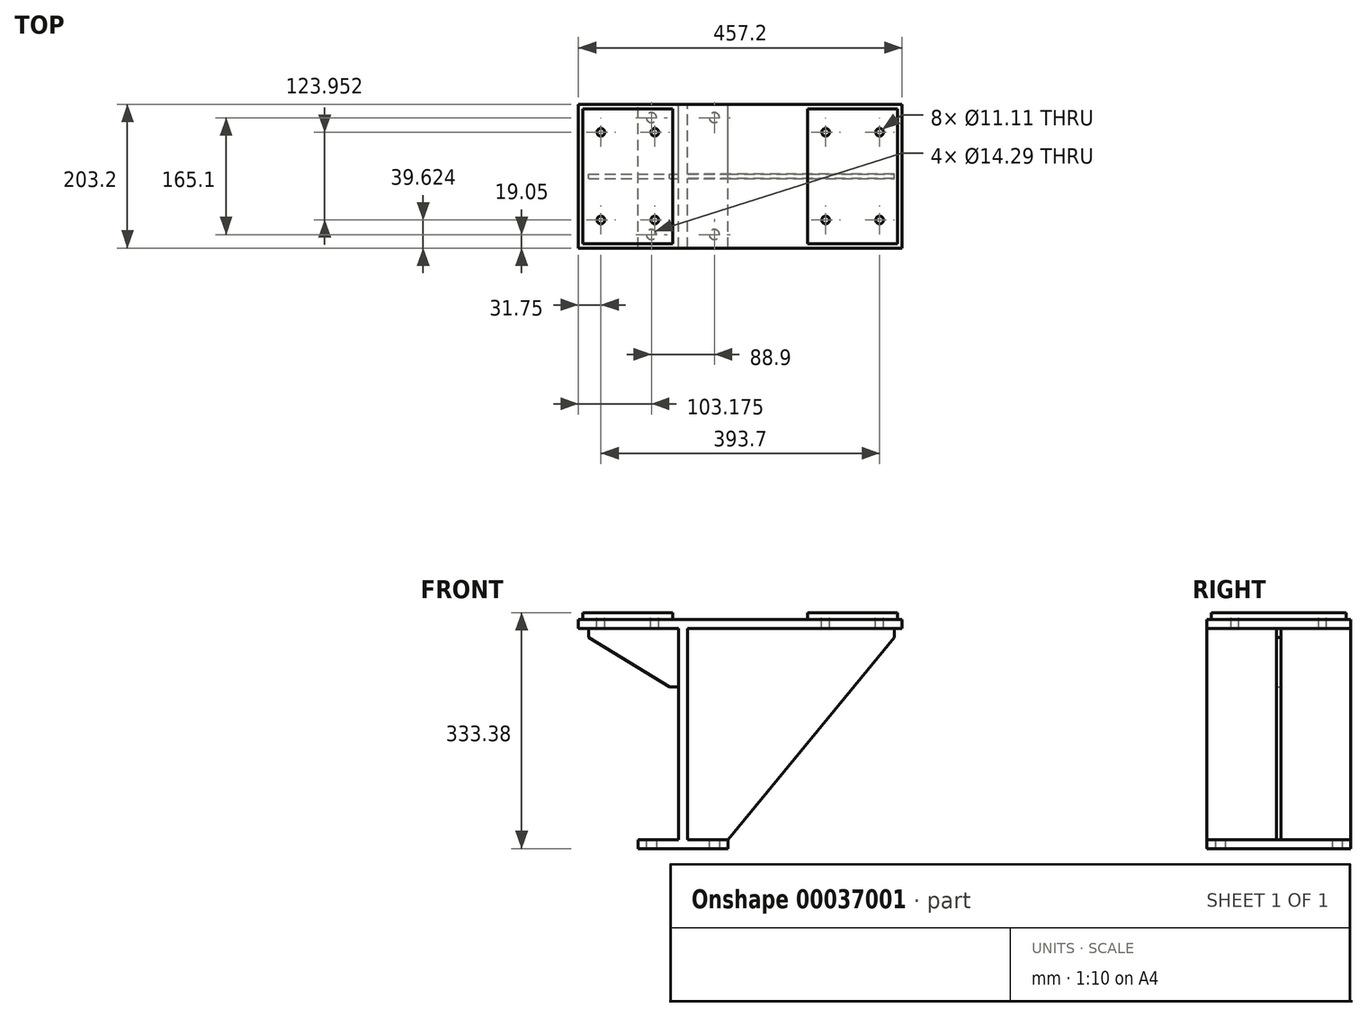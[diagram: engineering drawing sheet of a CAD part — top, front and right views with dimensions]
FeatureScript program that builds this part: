
annotation { "Feature Type Name" : "Feature", "Feature Type Description" : "" }
export const myFeature = defineFeature(function(context is Context, id is Id, definition is map)
    precondition{}
    {
        {
            var Q0;
            Q0=qCreatedBy(makeId("Top.planeOp"),FACE);
            var sketch = newSketch(context, id + "F0", { "sketchPlane" : qUnion([Q0])});
            skLineSegment(sketch, "E0.rect.bottom", {"start": v(-228.6, 101.6) * mm, "end": v(228.6, 101.6) * mm});
            skLineSegment(sketch, "E0.rect.top", {"start": v(-228.6, -101.6) * mm, "end": v(228.6, -101.6) * mm});
            skLineSegment(sketch, "E0.rect.left", {"start": v(-228.6, 101.6) * mm, "end": v(-228.6, -101.6) * mm});
            skLineSegment(sketch, "E0.rect.right", {"start": v(228.6, 101.6) * mm, "end": v(228.6, -101.6) * mm});
            skPoint(sketch, "E0.rect.middle", {"position": v(0, 0) * mm});
            skSolve(sketch);
        }
        {
            var Q0;
            Q0 = qSketchRegion(id + "F0", true);
            extrude(context, id + "F1", {"entities" : qUnion([Q0]), "oppositeDirection" : true, "depth" : 12.7 * mm});
        }
        {
            var Q0;
            Q0=makeQuery(id+"F1.opExtrude","CAP_FACE",FACE,{"disambiguationData":[OSD([sQuery(id+"F0.wireOp",EDGE,"E0.rect.bottom"),sQuery(id+"F0.wireOp",EDGE,"E0.rect.top"),sQuery(id+"F0.wireOp",EDGE,"E0.rect.left"),sQuery(id+"F0.wireOp",EDGE,"E0.rect.right")])],"isStart":true});
            var sketch = newSketch(context, id + "F2", { "sketchPlane" : qUnion([Q0])});
            skLineSegment(sketch, "E1.0", {"start": v(222.25, 95.25) * mm, "end": v(95.25, 95.25) * mm});
            skLineSegment(sketch, "E1.1", {"start": v(222.25, -95.25) * mm, "end": v(222.25, 95.25) * mm});
            skLineSegment(sketch, "E1.2", {"start": v(-222.25, -95.25) * mm, "end": v(-95.25, -95.25) * mm});
            skLineSegment(sketch, "E1.3", {"start": v(-222.25, 95.25) * mm, "end": v(-222.25, -95.25) * mm});
            skLineSegment(sketch, "E2.0", {"start": v(95.25, -95.25) * mm, "end": v(95.25, 95.25) * mm});
            skLineSegment(sketch, "E3.0", {"start": v(-95.25, 95.25) * mm, "end": v(-95.25, -95.25) * mm});
            skLineSegment(sketch, "E4.trimOffspring", {"start": v(-95.25, 95.25) * mm, "end": v(-222.25, 95.25) * mm});
            skLineSegment(sketch, "E5.trimOffspring", {"start": v(95.25, -95.25) * mm, "end": v(222.25, -95.25) * mm});
            skSolve(sketch);
        }
        {
            var Q0;
            Q0 = qSketchRegion(id + "F2", true);
            extrude(context, id + "F3", {"entities" : qUnion([Q0]), "operationType" : NewBodyOperationType.ADD, "depth" : 9.52 * mm});
        }
        {
            var Q0;
            Q0=makeQuery(id+"F3.opExtrude","CAP_FACE",FACE,{"disambiguationData":[OSD([sQuery(id+"F2.wireOp",EDGE,"E1.2"),sQuery(id+"F2.wireOp",EDGE,"E1.3"),sQuery(id+"F2.wireOp",EDGE,"E3.0"),sQuery(id+"F2.wireOp",EDGE,"E4.trimOffspring")])],"isStart":false});
            var sketch = newSketch(context, id + "F4", { "sketchPlane" : qUnion([Q0])});
            skLineSegment(sketch, "E6", {"start": v(-222.25, 0) * mm, "end": v(243.7, 0) * mm, "construction": true});
            skPoint(sketch, "E6.endSnap0", {"position": v(-95.25, 0) * mm});
            skLineSegment(sketch, "E7", {"start": v(-158.75, -95.25) * mm, "end": v(-158.75, 95.25) * mm, "construction": true});
            skLineSegment(sketch, "E8.0.0", {"start": v(222.25, -95.25) * mm, "end": v(222.25, 95.25) * mm, "construction": true});
            skLineSegment(sketch, "E8.0.1", {"start": v(222.25, 95.25) * mm, "end": v(95.25, 95.25) * mm, "construction": true});
            skLineSegment(sketch, "E8.0.2", {"start": v(95.25, 95.25) * mm, "end": v(95.25, -95.25) * mm, "construction": true});
            skLineSegment(sketch, "E8.0.3", {"start": v(95.25, -95.25) * mm, "end": v(222.25, -95.25) * mm, "construction": true});
            skLineSegment(sketch, "E9", {"start": v(158.75, -95.25) * mm, "end": v(158.75, 95.25) * mm, "construction": true});
            skLineSegment(sketch, "E10.0", {"start": v(-222.25, 61.98) * mm, "end": v(243.7, 61.98) * mm, "construction": true});
            skLineSegment(sketch, "E11.0", {"start": v(-222.25, -61.98) * mm, "end": v(243.7, -61.98) * mm, "construction": true});
            skLineSegment(sketch, "E12.0", {"start": v(-196.85, -95.25) * mm, "end": v(-196.85, 95.25) * mm, "construction": true});
            skLineSegment(sketch, "E13.0", {"start": v(-120.65, -95.25) * mm, "end": v(-120.65, 95.25) * mm, "construction": true});
            skLineSegment(sketch, "E14.0", {"start": v(120.65, -95.25) * mm, "end": v(120.65, 95.25) * mm, "construction": true});
            skLineSegment(sketch, "E15.0", {"start": v(196.85, -95.25) * mm, "end": v(196.85, 95.25) * mm, "construction": true});
            skPoint(sketch, "E16", {"position": v(-196.85, 61.98) * mm});
            skPoint(sketch, "E17", {"position": v(-120.65, 61.98) * mm});
            skPoint(sketch, "E18", {"position": v(-120.65, -61.98) * mm});
            skPoint(sketch, "E19", {"position": v(-196.85, -61.98) * mm});
            skPoint(sketch, "E20", {"position": v(120.65, 61.98) * mm});
            skPoint(sketch, "E21", {"position": v(196.85, 61.98) * mm});
            skPoint(sketch, "E22", {"position": v(196.85, -61.98) * mm});
            skPoint(sketch, "E23", {"position": v(120.65, -61.98) * mm});
            skSolve(sketch);
        }
        {
            var Q0;
            Q0=sQuery(id+"F4.wireOp",VERTEX,"E16");
            var Q1;
            Q1=sQuery(id+"F4.wireOp",VERTEX,"E17");
            var Q2;
            Q2=sQuery(id+"F4.wireOp",VERTEX,"E19");
            var Q3;
            Q3=sQuery(id+"F4.wireOp",VERTEX,"E18");
            var Q4;
            Q4=sQuery(id+"F4.wireOp",VERTEX,"E20");
            var Q5;
            Q5=sQuery(id+"F4.wireOp",VERTEX,"E21");
            var Q6;
            Q6=sQuery(id+"F4.wireOp",VERTEX,"E23");
            var Q7;
            Q7=sQuery(id+"F4.wireOp",VERTEX,"E22");
            var Q8;
            Q8=makeQuery(id+"F1.opExtrude","SWEPT_BODY",BODY,{"disambiguationData":[OSD([sQuery(id+"F0.wireOp",EDGE,"E0.rect.bottom"),sQuery(id+"F0.wireOp",EDGE,"E0.rect.top"),sQuery(id+"F0.wireOp",EDGE,"E0.rect.left"),sQuery(id+"F0.wireOp",EDGE,"E0.rect.right")])]});
            hole(context, id + "F5", {"style" : HoleStyle.SIMPLE, "holeDiameter" : 11.1 * mm, "endStyle" : HoleEndStyle.THROUGH, "locations" : qUnion([Q0, Q1, Q2, Q3, Q4, Q5, Q6, Q7]), "scope" : qUnion([Q8])});
        }
        {
            var Q0;
            Q0=qCreatedBy(makeId("Front.planeOp"),FACE);
            var sketch = newSketch(context, id + "F6", { "sketchPlane" : qUnion([Q0])});
            skLineSegment(sketch, "E24.0", {"start": v(-228.6, -12.7) * mm, "end": v(-228.6, 0) * mm, "construction": true});
            skLineSegment(sketch, "E25.0", {"start": v(-228.6, -12.7) * mm, "end": v(228.6, -12.7) * mm, "construction": true});
            skLineSegment(sketch, "E26", {"start": v(-228.6, -12.7) * mm, "end": v(-228.6, -311.15) * mm, "construction": true});
            skLineSegment(sketch, "E27.0", {"start": v(-80.98, -12.7) * mm, "end": v(-80.98, -311.15) * mm, "construction": true});
            skLineSegment(sketch, "E28.0", {"start": v(-87.33, -12.7) * mm, "end": v(-87.33, -311.15) * mm});
            skLineSegment(sketch, "E29.0", {"start": v(-74.63, -12.7) * mm, "end": v(-74.63, -311.15) * mm});
            skLineSegment(sketch, "E30.0", {"start": v(-214.33, -12.7) * mm, "end": v(-214.33, -25.4) * mm});
            skLineSegment(sketch, "E31.0", {"start": v(-228.6, -25.4) * mm, "end": v(-214.33, -25.4) * mm});
            skLineSegment(sketch, "E32.0", {"start": v(-228.6, -95.25) * mm, "end": v(-214.33, -95.25) * mm});
            skLineSegment(sketch, "E33", {"start": v(-214.33, -25.4) * mm, "end": v(-100.03, -95.25) * mm});
            skLineSegment(sketch, "E34.trimOffspring", {"start": v(-100.03, -95.25) * mm, "end": v(-87.33, -95.25) * mm});
            skLineSegment(sketch, "E35.trimOffspring", {"start": v(-214.33, -95.25) * mm, "end": v(-214.33, -311.15) * mm});
            skLineSegment(sketch, "E36", {"start": v(-214.33, -12.7) * mm, "end": v(-87.33, -12.7) * mm});
            skSolve(sketch);
        }
        {
            var Q0;
            Q0 = qSketchRegion(id + "F6", true);
            extrude(context, id + "F7", {"entities" : qUnion([Q0]), "operationType" : NewBodyOperationType.ADD, "endBound" : BoundingType.SYMMETRIC, "depth" : 6.35 * mm});
        }
        {
            var Q0;
            Q0=qCreatedBy(makeId("Front.planeOp"),FACE);
            var sketch = newSketch(context, id + "F8", { "sketchPlane" : qUnion([Q0])});
            skLineSegment(sketch, "E37.0", {"start": v(217.47, -12.7) * mm, "end": v(217.47, -311.15) * mm});
            skLineSegment(sketch, "E38.0", {"start": v(-74.63, -12.7) * mm, "end": v(-74.63, -311.15) * mm});
            skLineSegment(sketch, "E39.0", {"start": v(-17.48, -12.7) * mm, "end": v(-17.48, -311.15) * mm});
            skLineSegment(sketch, "E40.0", {"start": v(-228.6, -25.4) * mm, "end": v(228.6, -25.4) * mm});
            skLineSegment(sketch, "E41", {"start": v(-74.63, -311.15) * mm, "end": v(-17.48, -311.15) * mm});
            skLineSegment(sketch, "E42", {"start": v(-17.48, -311.15) * mm, "end": v(217.47, -25.4) * mm});
            skLineSegment(sketch, "E43", {"start": v(217.47, -25.4) * mm, "end": v(217.47, -12.7) * mm});
            skLineSegment(sketch, "E44", {"start": v(217.47, -12.7) * mm, "end": v(-74.63, -12.7) * mm});
            skSolve(sketch);
        }
        {
            var Q0;
            Q0 = qSketchRegion(id + "F8", true);
            extrude(context, id + "F9", {"entities" : qUnion([Q0]), "operationType" : NewBodyOperationType.ADD, "endBound" : BoundingType.SYMMETRIC, "depth" : 6.35 * mm});
        }
        {
            var Q0;
            Q0=qCreatedBy(makeId("Front.planeOp"),FACE);
            var sketch = newSketch(context, id + "F10", { "sketchPlane" : qUnion([Q0])});
            skLineSegment(sketch, "E45.0", {"start": v(-74.63, -12.7) * mm, "end": v(-74.63, -311.15) * mm});
            skLineSegment(sketch, "E46.0", {"start": v(-87.33, -12.7) * mm, "end": v(-87.33, -311.15) * mm});
            skLineSegment(sketch, "E47.0", {"start": v(-228.6, -12.7) * mm, "end": v(228.6, -12.7) * mm});
            skLineSegment(sketch, "E48", {"start": v(-87.33, -311.15) * mm, "end": v(-74.63, -311.15) * mm});
            skSolve(sketch);
        }
        {
            var Q0;
            Q0 = qSketchRegion(id + "F10", true);
            extrude(context, id + "F11", {"entities" : qUnion([Q0]), "operationType" : NewBodyOperationType.ADD, "endBound" : BoundingType.SYMMETRIC, "depth" : 203.2 * mm});
        }
        {
            var Q0;
            Q0=qCreatedBy(makeId("Front.planeOp"),FACE);
            var sketch = newSketch(context, id + "F12", { "sketchPlane" : qUnion([Q0])});
            skLineSegment(sketch, "E49.0", {"start": v(-74.63, -311.15) * mm, "end": v(-17.48, -311.15) * mm});
            skLineSegment(sketch, "E50.bottom", {"start": v(-17.48, -311.15) * mm, "end": v(-144.48, -311.15) * mm});
            skLineSegment(sketch, "E50.top", {"start": v(-17.48, -323.85) * mm, "end": v(-144.48, -323.85) * mm});
            skLineSegment(sketch, "E50.left", {"start": v(-17.48, -311.15) * mm, "end": v(-17.48, -323.85) * mm});
            skLineSegment(sketch, "E50.right", {"start": v(-144.48, -311.15) * mm, "end": v(-144.48, -323.85) * mm});
            skSolve(sketch);
        }
        {
            var Q0;
            Q0 = qSketchRegion(id + "F12", true);
            extrude(context, id + "F13", {"entities" : qUnion([Q0]), "operationType" : NewBodyOperationType.ADD, "endBound" : BoundingType.SYMMETRIC, "depth" : 203.2 * mm});
        }
        {
            var Q0;
            Q0=makeQuery(id+"F13.opExtrude","SWEPT_FACE",FACE,{"disambiguationData":[OSD([sQuery(id+"F12.wireOp",EDGE,"E50.top")])]});
            var sketch = newSketch(context, id + "F14", { "sketchPlane" : qUnion([Q0])});
            skLineSegment(sketch, "E51", {"start": v(-80.98, 101.6) * mm, "end": v(-80.98, -101.6) * mm, "construction": true});
            skLineSegment(sketch, "E52", {"start": v(-230.25, 0) * mm, "end": v(5.19, 0) * mm, "construction": true});
            skLineSegment(sketch, "E53.0", {"start": v(-125.43, 101.6) * mm, "end": v(-125.43, -101.6) * mm, "construction": true});
            skLineSegment(sketch, "E54.0", {"start": v(-230.25, 82.55) * mm, "end": v(5.19, 82.55) * mm, "construction": true});
            skPoint(sketch, "E55", {"position": v(-125.43, 82.55) * mm});
            skPoint(sketch, "E56.MirrorP", {"position": v(-36.53, 82.55) * mm});
            skPoint(sketch, "E57.MirrorP", {"position": v(-125.43, -82.55) * mm});
            skPoint(sketch, "E58.MirrorP", {"position": v(-36.53, -82.55) * mm});
            skSolve(sketch);
        }
        {
            var Q0;
            Q0=sQuery(id+"F14.wireOp",VERTEX,"E55");
            var Q1;
            Q1=sQuery(id+"F14.wireOp",VERTEX,"E57.MirrorP");
            var Q2;
            Q2=sQuery(id+"F14.wireOp",VERTEX,"E56.MirrorP");
            var Q3;
            Q3=sQuery(id+"F14.wireOp",VERTEX,"E58.MirrorP");
            var Q4;
            Q4=makeQuery(id+"F1.opExtrude","SWEPT_BODY",BODY,{"disambiguationData":[OSD([sQuery(id+"F0.wireOp",EDGE,"E0.rect.bottom"),sQuery(id+"F0.wireOp",EDGE,"E0.rect.top"),sQuery(id+"F0.wireOp",EDGE,"E0.rect.left"),sQuery(id+"F0.wireOp",EDGE,"E0.rect.right")])]});
            hole(context, id + "F15", {"style" : HoleStyle.SIMPLE, "holeDiameter" : 14.29 * mm, "endStyle" : HoleEndStyle.BLIND, "holeDepth" : 38.1 * mm, "locations" : qUnion([Q0, Q1, Q2, Q3]), "scope" : qUnion([Q4])});
        }
    });
